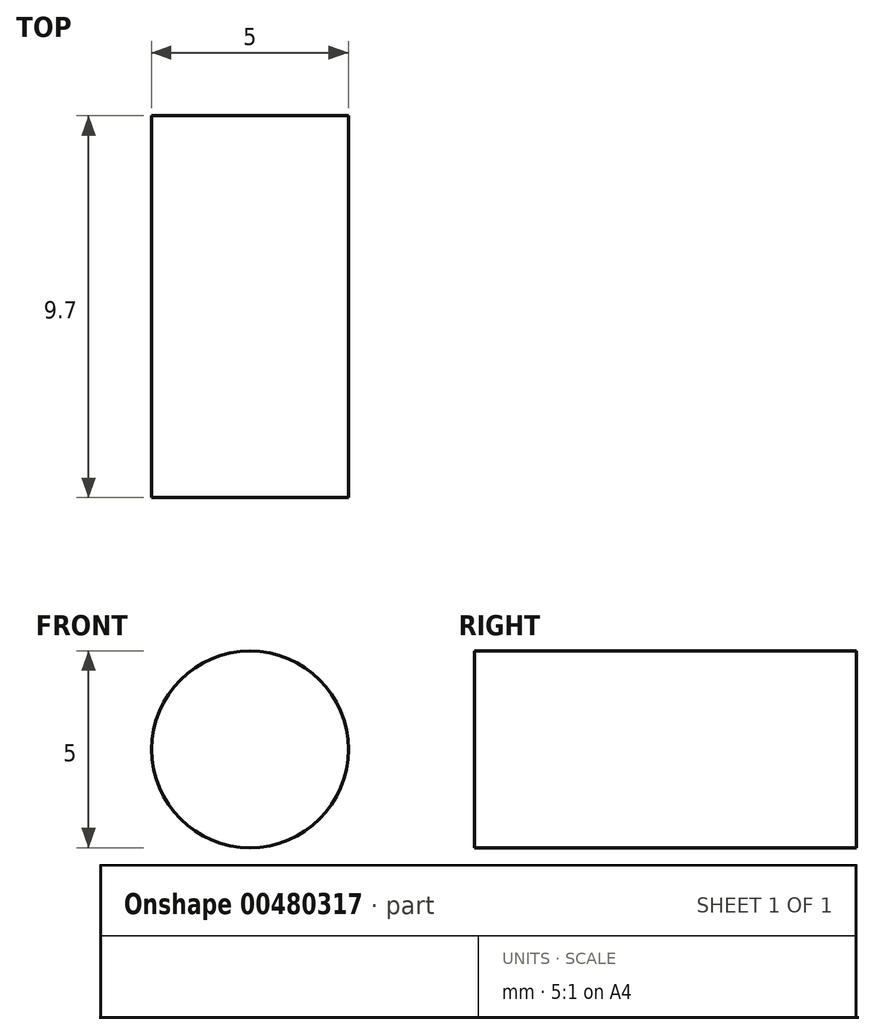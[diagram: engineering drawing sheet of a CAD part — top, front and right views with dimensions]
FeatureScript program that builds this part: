
annotation { "Feature Type Name" : "Feature", "Feature Type Description" : "" }
export const myFeature = defineFeature(function(context is Context, id is Id, definition is map)
    precondition{}
    {
        {
            var Q0;
            Q0=qCreatedBy(makeId("Front.planeOp"),FACE);
            var sketch = newSketch(context, id + "F0", { "sketchPlane" : qUnion([Q0])});
            skCircle(sketch, "E0", {"center": v(0, 0) * mm, "radius": 2.5 * mm});
            skSolve(sketch);
        }
        {
            var Q0;
            Q0=makeQuery(id+"F0.imprint","IMPRINT",FACE,{"disambiguationData":[TD([[makeQuery(id+"F0.imprint","IMPRINT",EDGE,{"derivedFrom":sQuery(id+"F0.wireOp",EDGE,"E0")}),1.0]])]});
            extrude(context, id + "F1", {"entities" : qUnion([Q0]), "depth" : 9.7 * mm, "offsetDistance" : 25 * mm, "symmetric" : true});
        }
    });
